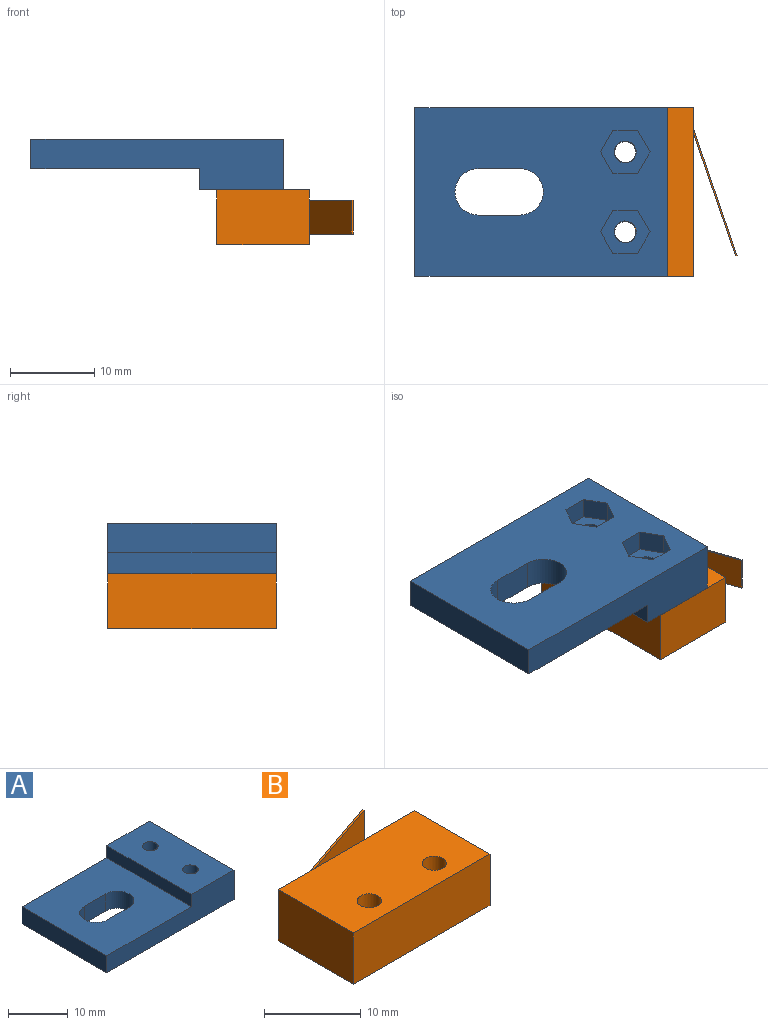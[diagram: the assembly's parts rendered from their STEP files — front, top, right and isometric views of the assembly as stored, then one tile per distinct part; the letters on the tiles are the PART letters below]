
ASSEMBLY  parts=2 mates=1
PART A: 28 faces, bbox 30x20x6 mm
  f0: plane 30x20mm, normal (0,0,-1), area 503.7mm2, adj f2,f3,f4,f5,f6,f7,f8,f9
  f1: plane 20x20mm, normal (0,0,1), area 348.7mm2, adj f2,f3,f4,f5,f6,f7,f9,f10
  f2: cylinder r=2.75mm len=5.5mm, axis (0,0,-1), area 30.2mm2, adj f0,f1,f3,f9
  f3: plane 5x3.5mm, normal (0,-1,0), area 17.5mm2, adj f0,f1,f2,f4
  f4: cylinder r=2.75mm len=5.5mm, axis (0,0,-1), area 30.2mm2, adj f0,f1,f3,f9
  f5: plane 30x6mm, normal (0,1,0), area 130mm2, adj f0,f1,f6,f8,f10,f11
  f6: plane 20x3.5mm, normal (-1,0,0), area 70mm2, adj f0,f1,f5,f7
  f7: plane 30x6mm, normal (0,-1,0), area 130mm2, adj f0,f1,f6,f8,f10,f11
  f8: plane 20x6mm, normal (1,0,0), area 120mm2, adj f0,f5,f7,f11
  f9: plane 5x3.5mm, normal (0,1,0), area 17.5mm2, adj f0,f1,f2,f4
  f10: plane 20x2.5mm, normal (-1,0,0), area 50mm2, adj f1,f5,f7,f11
  f11: plane 20x10mm, normal (0,0,1), area 189.4mm2, adj f5,f7,f8,f10,f12,f13
  f12: cylinder r=1.3mm len=3.5mm, axis (0,0,-1), area 28.6mm2, adj f11,f20
  f13: cylinder r=1.3mm len=3.5mm, axis (0,0,-1), area 28.6mm2, adj f11,f27
  f14: plane 2.55x2.5mm, normal (0.87,-0.5,0), area 7.4mm2, adj f0,f15,f19,f20
  f15: plane 2.94x2.5mm, normal (0,-1,0), area 7.4mm2, adj f0,f14,f16,f20
  f16: plane 2.55x2.5mm, normal (-0.87,-0.5,0), area 7.4mm2, adj f0,f15,f17,f20
  f17: plane 2.55x2.5mm, normal (-0.87,0.5,0), area 7.4mm2, adj f0,f16,f18,f20
  f18: plane 2.94x2.5mm, normal (0,1,0), area 7.4mm2, adj f0,f17,f19,f20
  f19: plane 2.55x2.5mm, normal (0.87,0.5,0), area 7.4mm2, adj f0,f14,f18,f20
  f20: plane 5.89x5.1mm, normal (0,0,-1), area 17.2mm2, adj f12,f14,f15,f16,f17,f18,f19
  f21: plane 2.94x2.5mm, normal (0,1,0), area 7.4mm2, adj f0,f22,f26,f27
  f22: plane 2.55x2.5mm, normal (0.87,0.5,0), area 7.4mm2, adj f0,f21,f23,f27
  f23: plane 2.55x2.5mm, normal (0.87,-0.5,0), area 7.4mm2, adj f0,f22,f24,f27
  f24: plane 2.94x2.5mm, normal (0,-1,0), area 7.4mm2, adj f0,f23,f25,f27
  f25: plane 2.55x2.5mm, normal (-0.87,-0.5,0), area 7.4mm2, adj f0,f24,f26,f27
  f26: plane 2.55x2.5mm, normal (-0.87,0.5,0), area 7.4mm2, adj f0,f21,f25,f27
  f27: plane 5.89x5.1mm, normal (0,0,-1), area 17.2mm2, adj f13,f21,f22,f23,f24,f25,f26
PART B: 13 faces, bbox 20x16.2x6.5 mm
  f0: plane 20x6.5mm, normal (0,1,0), area 127.5mm2, adj f1,f3,f6,f7,f8,f9,f11,f12
  f1: plane 11x6.5mm, normal (-1,0,0), area 71.5mm2, adj f0,f2,f6,f7
  f2: plane 20x6.5mm, normal (0,-1,0), area 130mm2, adj f1,f3,f6,f7
  f3: plane 11x6.5mm, normal (1,0,0), area 71.5mm2, adj f0,f2,f6,f7
  f4: cylinder r=1.25mm len=6.5mm, axis (0,0,-1), area 51.1mm2, adj f6,f7
  f5: cylinder r=1.25mm len=6.5mm, axis (0,0,-1), area 51.1mm2, adj f6,f7
  f6: plane 20x11mm, normal (0,0,1), area 210.2mm2, adj f0,f1,f2,f3,f4,f5
  f7: plane 20x11mm, normal (0,0,-1), area 210.2mm2, adj f0,f1,f2,f3,f4,f5
  f8: plane 15.14x5.19mm, normal (-0.32,0.95,0), area 64mm2, adj f0,f10,f11,f12
  f9: plane 14.58x5mm, normal (0.32,-0.95,0), area 61.7mm2, adj f0,f10,f11,f12
  f10: plane 4x0.19mm, normal (0.95,0.32,0), area 0.8mm2, adj f8,f9,f11,f12
  f11: plane 15.2x5.19mm, normal (0,0,1), area 3.1mm2, adj f0,f8,f9,f10
  f12: plane 15.2x5.19mm, normal (0,0,-1), area 3.1mm2, adj f0,f8,f9,f10
PLACE A rot(axis=(1,0,0),180deg) t=(-6.07,11.9,30.65)mm
PLACE B rot(axis=(0,0,-1),90deg) t=(16.03,11.9,18.15)mm
MATE fastened A.f13 <-> B.f4  axis (0,0,-1) through (18.93,6.65,24.65)mm
